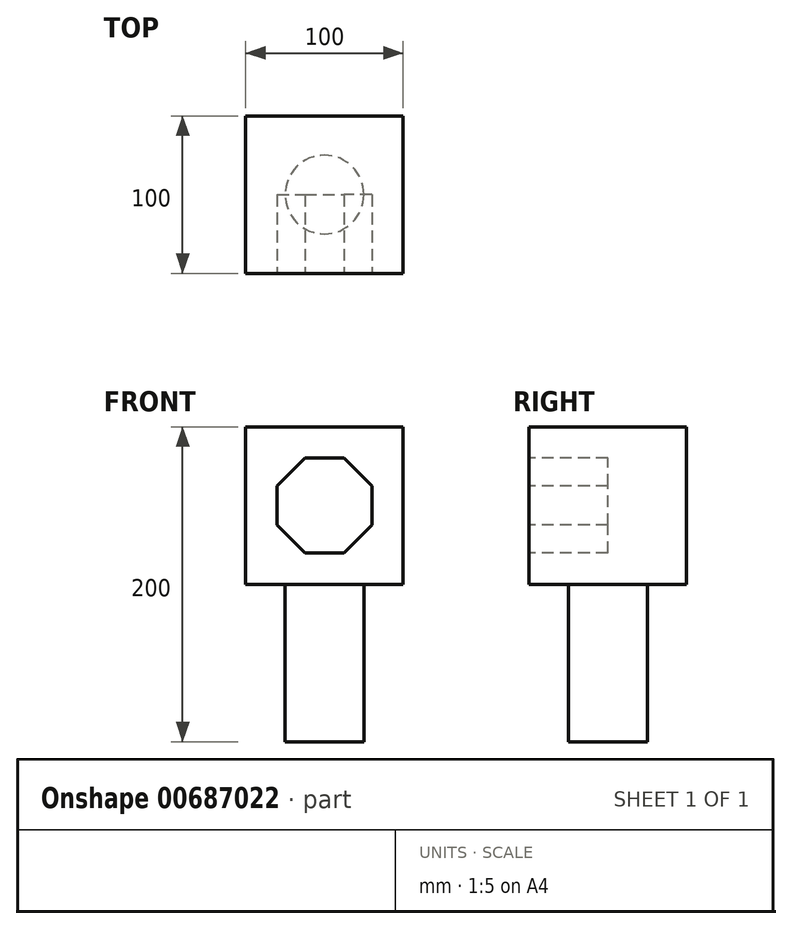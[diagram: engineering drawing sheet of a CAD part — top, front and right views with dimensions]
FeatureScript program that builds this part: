
annotation { "Feature Type Name" : "Feature", "Feature Type Description" : "" }
export const myFeature = defineFeature(function(context is Context, id is Id, definition is map)
    precondition{}
    {
        {
            var Q0;
            Q0=qCreatedBy(makeId("Top.planeOp"),FACE);
            var sketch = newSketch(context, id + "F0", { "sketchPlane" : qUnion([Q0])});
            skLineSegment(sketch, "E0.bottom", {"start": v(50, 50) * mm, "end": v(-50, 50) * mm});
            skLineSegment(sketch, "E0.top", {"start": v(50, -50) * mm, "end": v(-50, -50) * mm});
            skLineSegment(sketch, "E0.left", {"start": v(50, 50) * mm, "end": v(50, -50) * mm});
            skLineSegment(sketch, "E0.right", {"start": v(-50, 50) * mm, "end": v(-50, -50) * mm});
            skPoint(sketch, "E0.middle", {"position": v(0, 0) * mm});
            skSolve(sketch);
        }
        {
            var Q0;
            Q0 = qSketchRegion(id + "F0", true);
            extrude(context, id + "F1", {"entities" : qUnion([Q0]), "depth" : 100 * mm, "offsetDistance" : 25 * mm});
        }
        {
            var Q0;
            Q0=makeQuery(id+"F1.opExtrude","CAP_FACE",FACE,{"disambiguationData":[OSD([sQuery(id+"F0.wireOp",EDGE,"E0.bottom"),sQuery(id+"F0.wireOp",EDGE,"E0.top"),sQuery(id+"F0.wireOp",EDGE,"E0.left"),sQuery(id+"F0.wireOp",EDGE,"E0.right")])],"isStart":true});
            var sketch = newSketch(context, id + "F2", { "sketchPlane" : qUnion([Q0])});
            skCircle(sketch, "E1", {"center": v(0, 0) * mm, "radius": 25 * mm});
            skSolve(sketch);
        }
        {
            var Q0;
            Q0 = qSketchRegion(id + "F2", true);
            extrude(context, id + "F3", {"entities" : qUnion([Q0]), "operationType" : NewBodyOperationType.ADD, "depth" : 100 * mm, "offsetDistance" : 25 * mm});
        }
        {
            var Q0;
            Q0=makeQuery(id+"F1.opExtrude","SWEPT_FACE",FACE,{"disambiguationData":[OSD([sQuery(id+"F0.wireOp",EDGE,"E0.top")])]});
            var sketch = newSketch(context, id + "F4", { "sketchPlane" : qUnion([Q0])});
            skCircle(sketch, "E2.cCircle", {"center": v(0, 50) * mm, "radius": 30.18 * mm, "construction": true});
            skLineSegment(sketch, "E2.0", {"start": v(-12.5, 80.18) * mm, "end": v(12.5, 80.18) * mm});
            skLineSegment(sketch, "E2.1", {"start": v(12.5, 80.18) * mm, "end": v(30.18, 62.5) * mm});
            skLineSegment(sketch, "E2.2", {"start": v(30.18, 62.5) * mm, "end": v(30.18, 37.5) * mm});
            skLineSegment(sketch, "E2.3", {"start": v(30.18, 37.5) * mm, "end": v(12.5, 19.82) * mm});
            skLineSegment(sketch, "E2.4", {"start": v(12.5, 19.82) * mm, "end": v(-12.5, 19.82) * mm});
            skLineSegment(sketch, "E2.5", {"start": v(-12.5, 19.82) * mm, "end": v(-30.18, 37.5) * mm});
            skLineSegment(sketch, "E2.6", {"start": v(-30.18, 37.5) * mm, "end": v(-30.18, 62.5) * mm});
            skLineSegment(sketch, "E2.7", {"start": v(-30.18, 62.5) * mm, "end": v(-12.5, 80.18) * mm});
            skPoint(sketch, "E2.0.midPoint", {"position": v(0, 80.18) * mm});
            skSolve(sketch);
        }
        {
            var Q0;
            Q0 = qSketchRegion(id + "F4", true);
            extrude(context, id + "F5", {"entities" : qUnion([Q0]), "operationType" : NewBodyOperationType.REMOVE, "oppositeDirection" : true, "depth" : 50 * mm, "offsetDistance" : 25 * mm});
        }
    });
